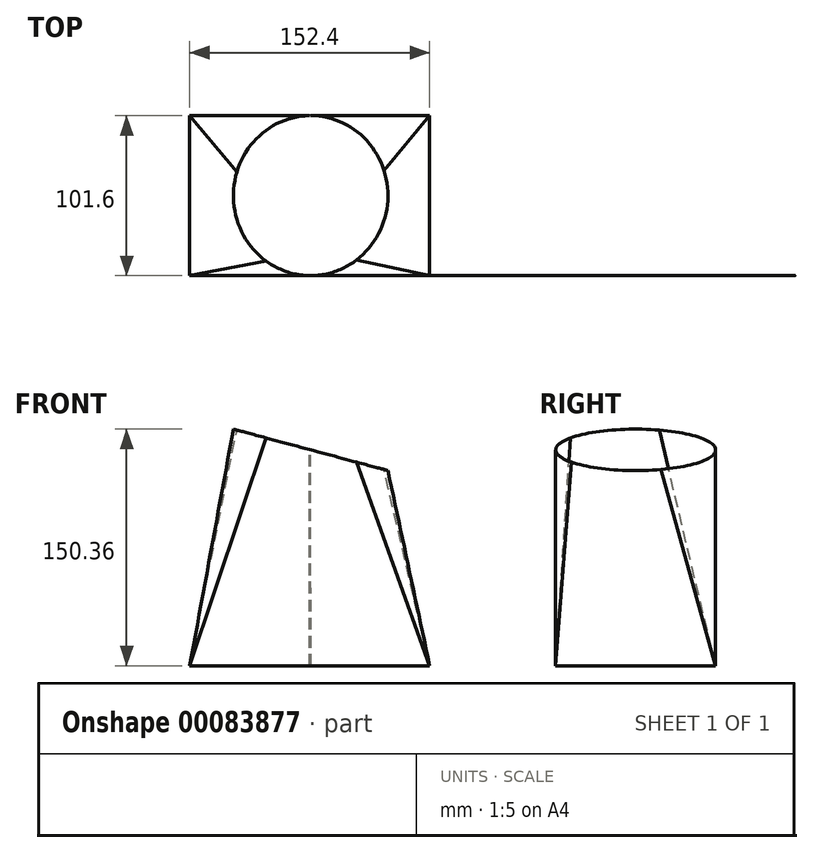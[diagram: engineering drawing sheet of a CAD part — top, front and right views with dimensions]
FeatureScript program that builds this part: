
annotation { "Feature Type Name" : "Feature", "Feature Type Description" : "" }
export const myFeature = defineFeature(function(context is Context, id is Id, definition is map)
    precondition{}
    {
        {
            var Q0;
            Q0=qCreatedBy(makeId("Top.planeOp"),FACE);
            var sketch = newSketch(context, id + "F0", { "sketchPlane" : qUnion([Q0])});
            skLineSegment(sketch, "E0.bottom", {"start": v(76.2, -50.8) * mm, "end": v(-76.2, -50.8) * mm});
            skLineSegment(sketch, "E0.top", {"start": v(76.2, 50.8) * mm, "end": v(0.83, 50.8) * mm});
            skLineSegment(sketch, "E0.left", {"start": v(76.2, -50.8) * mm, "end": v(76.2, 50.8) * mm});
            skLineSegment(sketch, "E0.right", {"start": v(-76.2, -50.8) * mm, "end": v(-76.2, 50.8) * mm});
            skPoint(sketch, "E0.middle", {"position": v(0, 0) * mm});
            skLineSegment(sketch, "E1.trimOffspring", {"start": v(0, 50.8) * mm, "end": v(-76.2, 50.8) * mm});
            skSolve(sketch);
        }
        {
            var Q0;
            Q0=qCreatedBy(makeId("Top.planeOp"),FACE);
            var Q1;
            Q1=sQuery(id+"F0.wireOp",EDGE,"E0.right");
            cPlane(context, id + "F1", {"entities" : qUnion([Q0, Q1]), "cplaneType" : CPlaneType.LINE_ANGLE, "offset" : 152.4 * mm, "angle" : 15 * degree, "width" : 152.4 * mm, "height" : 152.4 * mm});
        }
        {
            var Q0;
            Q0=qCreatedBy(id+"F1.planeOp",FACE);
            cPlane(context, id + "F2", {"entities" : qUnion([Q0]), "cplaneType" : CPlaneType.OFFSET, "offset" : 152.4 * mm, "oppositeDirection" : true, "width" : 152.4 * mm, "height" : 152.4 * mm});
        }
        {
            var Q0;
            Q0=qCreatedBy(id+"F2.planeOp",FACE);
            var sketch = newSketch(context, id + "F3", { "sketchPlane" : qUnion([Q0])});
            skArc(sketch, "E2", {"start": v(-35.2, -50.8) * mm, "mid": v(-34.4, 50.8) * mm, "end": v(-35.86, -50.8) * mm});
            skSolve(sketch);
        }
        {
            var Q0;
            Q0 = qConstructionFilter(qBodyType(qCreatedBy(id + "F0" ,EDGE), BodyType.WIRE), ConstructionObject.NO);
            var Q1;
            Q1 = qConstructionFilter(qBodyType(qCreatedBy(id + "F3" ,EDGE), BodyType.WIRE), ConstructionObject.NO);
            loft(context, id + "F4", {"bodyType" : ToolBodyType.SURFACE, "wireProfilesArray" : [{ "wireProfileEntities" : qUnion([Q0]) }, { "wireProfileEntities" : qUnion([Q1]) }]});
        }
    });
